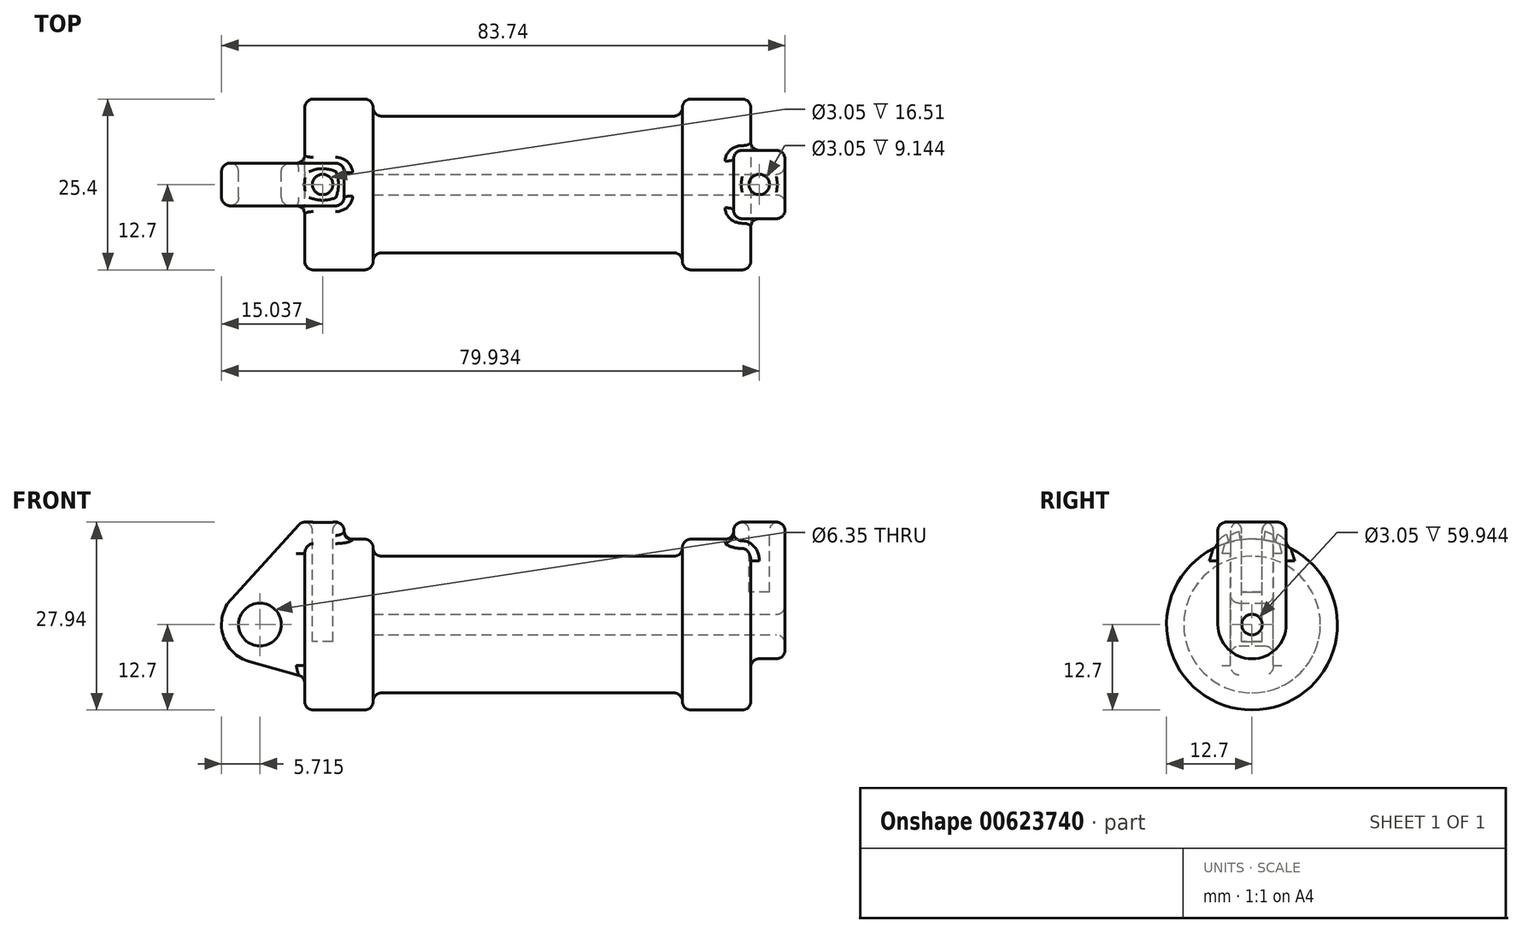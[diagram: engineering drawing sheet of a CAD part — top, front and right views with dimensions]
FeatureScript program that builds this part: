
annotation { "Feature Type Name" : "Feature", "Feature Type Description" : "" }
export const myFeature = defineFeature(function(context is Context, id is Id, definition is map)
    precondition{}
    {
        {
            var Q0;
            Q0=qCreatedBy(makeId("Front.planeOp"),FACE);
            var sketch = newSketch(context, id + "F0", { "sketchPlane" : qUnion([Q0])});
            skLineSegment(sketch, "E0", {"start": v(0, 0) * mm, "end": v(0, 12.7) * mm});
            skLineSegment(sketch, "E1", {"start": v(0, 12.7) * mm, "end": v(10.16, 12.7) * mm});
            skLineSegment(sketch, "E2", {"start": v(10.16, 12.7) * mm, "end": v(10.16, 10.16) * mm});
            skLineSegment(sketch, "E3", {"start": v(10.16, 10.16) * mm, "end": v(56.13, 10.16) * mm});
            skLineSegment(sketch, "E4", {"start": v(56.13, 10.16) * mm, "end": v(56.13, 12.7) * mm});
            skLineSegment(sketch, "E5", {"start": v(56.13, 12.7) * mm, "end": v(66.3, 12.7) * mm});
            skLineSegment(sketch, "E6", {"start": v(66.3, 12.7) * mm, "end": v(66.3, 0) * mm});
            skLineSegment(sketch, "E7", {"start": v(66.3, 0) * mm, "end": v(0, 0) * mm});
            skLineSegment(sketch, "E8", {"start": v(5.84, 15.24) * mm, "end": v(-0.5, 15.24) * mm});
            skLineSegment(sketch, "E9", {"start": v(-0.5, 15.24) * mm, "end": v(-10.88, 3.85) * mm});
            skLineSegment(sketch, "E10", {"start": v(0, 0) * mm, "end": v(-6.65, 0) * mm});
            skCircle(sketch, "E11", {"center": v(-6.65, 0) * mm, "radius": 5.72 * mm});
            skCircle(sketch, "E12", {"center": v(-6.65, 0) * mm, "radius": 3.18 * mm});
            skLineSegment(sketch, "E13", {"start": v(5.84, 15.24) * mm, "end": v(5.84, -9.4) * mm});
            skLineSegment(sketch, "E14", {"start": v(5.84, -9.4) * mm, "end": v(-8.18, -5.5) * mm});
            skSolve(sketch);
        }
        {
            var Q0;
            {var subQ1=sQuery(id+"F0.wireOp",EDGE,"E0");Q0=makeQuery(id+"F0.imprint","IMPRINT",FACE,{"disambiguationData":[TD([[makeQuery(id+"F0.imprint","IMPRINT",EDGE,{"derivedFrom":subQ1}),1.0]])]});}
            var Q1;
            {var subQ0=sQuery(id+"F0.wireOp",EDGE,"E14");Q1=makeQuery(id+"F0.imprint","IMPRINT",FACE,{"disambiguationData":[TD([[makeQuery(id+"F0.imprint","IMPRINT",EDGE,{"derivedFrom":subQ0}),-1.0]])]});}
            var Q2;
            {var subQ0=sQuery(id+"F0.wireOp",EDGE,"E0");Q2=makeQuery(id+"F0.imprint","IMPRINT",FACE,{"disambiguationData":[TD([[makeQuery(id+"F0.imprint","IMPRINT",EDGE,{"derivedFrom":subQ0}),-1.0]])]});}
            var Q3;
            {var subQ5=sQuery(id+"F0.wireOp",EDGE,"E12");Q3=makeQuery(id+"F0.imprint","IMPRINT",FACE,{"disambiguationData":[TD([[makeQuery(id+"F0.imprint","IMPRINT",EDGE,{"derivedFrom":subQ5}),-1.0]])]});}
            extrude(context, id + "F1", {"entities" : qUnion([Q0, Q1, Q2, Q3]), "endBound" : BoundingType.SYMMETRIC, "depth" : 6.35 * mm, "offsetDistance" : 25.4 * mm});
        }
        {
            var Q0;
            {var subQ0=sQuery(id+"F0.wireOp",EDGE,"E0");Q0=makeQuery(id+"F0.imprint","IMPRINT",FACE,{"disambiguationData":[TD([[makeQuery(id+"F0.imprint","IMPRINT",EDGE,{"derivedFrom":subQ0}),-1.0]])]});}
            var Q1;
            {var subQ0=sQuery(id+"F0.wireOp",EDGE,"E2");Q1=makeQuery(id+"F0.imprint","IMPRINT",FACE,{"disambiguationData":[TD([[makeQuery(id+"F0.imprint","IMPRINT",EDGE,{"derivedFrom":subQ0}),-1.0]])]});}
            var Q2;
            Q2=sQuery(id+"F0.wireOp",EDGE,"E7");
            revolve(context, id + "F2", {"operationType" : NewBodyOperationType.ADD, "entities" : qUnion([Q0, Q1]), "axis" : qUnion([Q2]), "revolveType" : RevolveType.FULL});
        }
        {
            var Q0;
            Q0=makeQuery(id+"F2.opRevolve","SWEPT_FACE",FACE,{"disambiguationData":[OSD([sQuery(id+"F0.wireOp",EDGE,"E6")])]});
            var sketch = newSketch(context, id + "F3", { "sketchPlane" : qUnion([Q0])});
            skCircle(sketch, "E15.0", {"center": v(0, 0) * mm, "radius": 12.7 * mm});
            skLineSegment(sketch, "E15.1", {"start": v(3.18, 15.24) * mm, "end": v(3.18, 12.3) * mm});
            skLineSegment(sketch, "E15.2", {"start": v(-3.18, 15.24) * mm, "end": v(3.17, 15.24) * mm});
            skLineSegment(sketch, "E15.3", {"start": v(-3.18, 15.24) * mm, "end": v(-3.18, 12.3) * mm});
            skLineSegment(sketch, "E16", {"start": v(0, 15.24) * mm, "end": v(0, -12.7) * mm, "construction": true});
            skCircle(sketch, "E17", {"center": v(0, 0) * mm, "radius": 1.52 * mm});
            skCircle(sketch, "E18", {"center": v(0, 0) * mm, "radius": 5.08 * mm});
            skLineSegment(sketch, "E19", {"start": v(5.08, 0) * mm, "end": v(5.08, 15.24) * mm});
            skLineSegment(sketch, "E20", {"start": v(5.08, 15.24) * mm, "end": v(3.18, 15.24) * mm});
            skLineSegment(sketch, "E21.MirrorCS", {"start": v(-5.08, 0) * mm, "end": v(-5.08, 15.24) * mm});
            skLineSegment(sketch, "E22.MirrorCS", {"start": v(-5.08, 15.24) * mm, "end": v(-3.18, 15.24) * mm});
            skSolve(sketch);
        }
        {
            var Q0;
            {var subQ0=sQuery(id+"F3.wireOp",EDGE,"E15.1");Q0=makeQuery(id+"F3.imprint","IMPRINT",FACE,{"disambiguationData":[TD([[makeQuery(id+"F3.imprint","IMPRINT",EDGE,{"derivedFrom":subQ0}),1.0]])]});}
            var Q1;
            {var subQ0=sQuery(id+"F3.wireOp",EDGE,"E15.1");Q1=makeQuery(id+"F3.imprint","IMPRINT",FACE,{"disambiguationData":[TD([[makeQuery(id+"F3.imprint","IMPRINT",EDGE,{"derivedFrom":subQ0}),-1.0]])]});}
            var Q2;
            {var subQ0=sQuery(id+"F3.wireOp",EDGE,"E15.3");Q2=makeQuery(id+"F3.imprint","IMPRINT",FACE,{"disambiguationData":[TD([[makeQuery(id+"F3.imprint","IMPRINT",EDGE,{"derivedFrom":subQ0}),-1.0]])]});}
            extrude(context, id + "F4", {"entities" : qUnion([Q0, Q1, Q2]), "operationType" : NewBodyOperationType.ADD, "oppositeDirection" : true, "depth" : 2.54 * mm, "offsetDistance" : 25.4 * mm});
        }
        {
            var Q0;
            Q0=makeQuery(id+"F3.imprint","IMPRINT",FACE,{"disambiguationData":[TD([[makeQuery(id+"F3.imprint","IMPRINT",EDGE,{"derivedFrom":sQuery(id+"F3.wireOp",EDGE,"E17")}),1.0]])]});
            var Q1;
            Q1=makeQuery(id+"F2.opRevolve","SWEPT_FACE",FACE,{"disambiguationData":[OSD([sQuery(id+"F0.wireOp",EDGE,"E2")])]});
            extrude(context, id + "F5", {"entities" : qUnion([Q0]), "operationType" : NewBodyOperationType.REMOVE, "endBound" : BoundingType.UP_TO_SURFACE, "oppositeDirection" : true, "depth" : 25.4 * mm, "endBoundEntityFace" : qUnion([Q1]), "offsetDistance" : 25.4 * mm});
        }
        {
            var Q0;
            {var subQ0=sQuery(id+"F3.wireOp",EDGE,"E15.3");Q0=makeQuery(id+"F3.imprint","IMPRINT",FACE,{"disambiguationData":[TD([[makeQuery(id+"F3.imprint","IMPRINT",EDGE,{"derivedFrom":subQ0}),-1.0]])]});}
            var Q1;
            {var subQ0=sQuery(id+"F3.wireOp",EDGE,"E15.1");Q1=makeQuery(id+"F3.imprint","IMPRINT",FACE,{"disambiguationData":[TD([[makeQuery(id+"F3.imprint","IMPRINT",EDGE,{"derivedFrom":subQ0}),-1.0]])]});}
            var Q2;
            {var subQ0=sQuery(id+"F3.wireOp",EDGE,"E15.1");Q2=makeQuery(id+"F3.imprint","IMPRINT",FACE,{"disambiguationData":[TD([[makeQuery(id+"F3.imprint","IMPRINT",EDGE,{"derivedFrom":subQ0}),1.0]])]});}
            var Q3;
            {var subQ5=sQuery(id+"F3.wireOp",EDGE,"E15.0");var subQ8=makeQuery(id+"F3.imprint","INTERSECT",VERTEX,{"derivedFrom":[subQ5,sQuery(id+"F3.wireOp",EDGE,"E15.1")]});Q3=makeQuery(id+"F3.imprint","IMPRINT",FACE,{"disambiguationData":[TD([[makeQuery(id+"F3.imprint","IMPRINT",EDGE,{"disambiguationData":[TD([[subQ8,1.0]])],"derivedFrom":subQ5}),1.0]])]});}
            var Q4;
            Q4=makeQuery(id+"F3.imprint","IMPRINT",FACE,{"disambiguationData":[TD([[makeQuery(id+"F3.imprint","IMPRINT",EDGE,{"derivedFrom":sQuery(id+"F3.wireOp",EDGE,"E17")}),-1.0]])]});
            extrude(context, id + "F6", {"entities" : qUnion([Q0, Q1, Q2, Q3, Q4]), "operationType" : NewBodyOperationType.ADD, "depth" : 5.08 * mm, "offsetDistance" : 25.4 * mm});
        }
        {
            var Q0;
            Q0=makeQuery(id+"F1.opExtrude","SWEPT_FACE",FACE,{"disambiguationData":[OSD([sQuery(id+"F0.wireOp",EDGE,"E8")])]});
            var sketch = newSketch(context, id + "F7", { "sketchPlane" : qUnion([Q0])});
            skCircle(sketch, "E23", {"center": v(2.67, 0) * mm, "radius": 1.52 * mm});
            skSolve(sketch);
        }
        {
            var Q0;
            Q0=makeQuery(id+"F7.imprint","IMPRINT",FACE,{"disambiguationData":[TD([[makeQuery(id+"F7.imprint","IMPRINT",EDGE,{"derivedFrom":sQuery(id+"F7.wireOp",EDGE,"E23")}),1.0]])]});
            extrude(context, id + "F8", {"entities" : qUnion([Q0]), "operationType" : NewBodyOperationType.REMOVE, "oppositeDirection" : true, "depth" : 17.78 * mm, "offsetDistance" : 25.4 * mm});
        }
        {
            var Q0;
            {var subQ0=sQuery(id+"F3.wireOp",EDGE,"E22.MirrorCS");var subQ1=sQuery(id+"F3.wireOp",EDGE,"E20");var subQ2=sQuery(id+"F3.wireOp",EDGE,"E15.2");Q0=makeQuery(id+"F6.boolean.opBoolean","MERGE",FACE,{"derivedFrom":[makeQuery(id+"F4.opExtrude","SWEPT_FACE",FACE,{"disambiguationData":[OSD([subQ2,subQ1,subQ0])]}),makeQuery(id+"F6.opExtrude","SWEPT_FACE",FACE,{"disambiguationData":[OSD([subQ2,subQ1,subQ0])]})]});}
            var sketch = newSketch(context, id + "F9", { "sketchPlane" : qUnion([Q0])});
            skLineSegment(sketch, "E24", {"start": v(63.75, 0) * mm, "end": v(71.37, 0) * mm, "construction": true});
            skCircle(sketch, "E25", {"center": v(67.56, 0) * mm, "radius": 1.52 * mm});
            skSolve(sketch);
        }
        {
            var Q0;
            Q0=makeQuery(id+"F9.imprint","IMPRINT",FACE,{"disambiguationData":[TD([[makeQuery(id+"F9.imprint","IMPRINT",EDGE,{"derivedFrom":sQuery(id+"F9.wireOp",EDGE,"E25")}),1.0]])]});
            extrude(context, id + "F10", {"entities" : qUnion([Q0]), "operationType" : NewBodyOperationType.REMOVE, "oppositeDirection" : true, "depth" : 10.4 * mm, "offsetDistance" : 25.4 * mm});
        }
        {
            var Q0;
            Q0=makeQuery(id+"F2.opRevolve","SWEPT_FACE",FACE,{"disambiguationData":[OSD([sQuery(id+"F0.wireOp",EDGE,"E3")])]});
            var Q1;
            Q1=makeQuery(id+"F6.opExtrude","CAP_FACE",FACE,{"disambiguationData":[OSD([sQuery(id+"F3.wireOp",EDGE,"E15.2"),sQuery(id+"F3.wireOp",EDGE,"E17"),sQuery(id+"F3.wireOp",EDGE,"E18"),sQuery(id+"F3.wireOp",EDGE,"E19"),sQuery(id+"F3.wireOp",EDGE,"E20"),sQuery(id+"F3.wireOp",EDGE,"E21.MirrorCS"),sQuery(id+"F3.wireOp",EDGE,"E22.MirrorCS")])],"isStart":false});
            var Q2;
            {var subQ0=sQuery(id+"F3.wireOp",EDGE,"E22.MirrorCS");var subQ1=sQuery(id+"F3.wireOp",EDGE,"E20");var subQ2=sQuery(id+"F3.wireOp",EDGE,"E15.2");Q2=makeQuery(id+"F6.boolean.opBoolean","MERGE",FACE,{"derivedFrom":[makeQuery(id+"F4.opExtrude","SWEPT_FACE",FACE,{"disambiguationData":[OSD([subQ2,subQ1,subQ0])]}),makeQuery(id+"F6.opExtrude","SWEPT_FACE",FACE,{"disambiguationData":[OSD([subQ2,subQ1,subQ0])]})]});}
            var Q3;
            Q3=makeQuery(id+"F4.boolean.opBoolean","MERGE",FACE,{"derivedFrom":[makeQuery(id+"F2.opRevolve","SWEPT_FACE",FACE,{"disambiguationData":[OSD([sQuery(id+"F0.wireOp",EDGE,"E6")])]}),makeQuery(id+"F4.opExtrude","CAP_FACE",FACE,{"disambiguationData":[OSD([sQuery(id+"F3.wireOp",EDGE,"E15.0"),sQuery(id+"F3.wireOp",EDGE,"E15.2"),sQuery(id+"F3.wireOp",EDGE,"E19"),sQuery(id+"F3.wireOp",EDGE,"E20"),sQuery(id+"F3.wireOp",EDGE,"E21.MirrorCS"),sQuery(id+"F3.wireOp",EDGE,"E22.MirrorCS")])],"isStart":true})]});
            var Q4;
            Q4=makeQuery(id+"F2.opRevolve","SWEPT_FACE",FACE,{"disambiguationData":[OSD([sQuery(id+"F0.wireOp",EDGE,"E5")])]});
            var Q5;
            Q5=makeQuery(id+"F2.opRevolve","SWEPT_FACE",FACE,{"disambiguationData":[OSD([sQuery(id+"F0.wireOp",EDGE,"E1")])]});
            var Q6;
            Q6=makeQuery(id+"F2.opRevolve","SWEPT_FACE",FACE,{"disambiguationData":[OSD([sQuery(id+"F0.wireOp",EDGE,"E0")])]});
            var Q7;
            Q7=makeQuery(id+"F1.opExtrude","CAP_FACE",FACE,{"disambiguationData":[OSD([sQuery(id+"F0.wireOp",EDGE,"E8"),sQuery(id+"F0.wireOp",EDGE,"E9"),sQuery(id+"F0.wireOp",EDGE,"E11"),sQuery(id+"F0.wireOp",EDGE,"E12"),sQuery(id+"F0.wireOp",EDGE,"E13"),sQuery(id+"F0.wireOp",EDGE,"E14")])],"isStart":false});
            var Q8;
            Q8=makeQuery(id+"F1.opExtrude","CAP_FACE",FACE,{"disambiguationData":[OSD([sQuery(id+"F0.wireOp",EDGE,"E8"),sQuery(id+"F0.wireOp",EDGE,"E9"),sQuery(id+"F0.wireOp",EDGE,"E11"),sQuery(id+"F0.wireOp",EDGE,"E12"),sQuery(id+"F0.wireOp",EDGE,"E13"),sQuery(id+"F0.wireOp",EDGE,"E14")])],"isStart":true});
            var Q9;
            Q9=makeQuery(id+"F1.opExtrude","SWEPT_FACE",FACE,{"disambiguationData":[OSD([sQuery(id+"F0.wireOp",EDGE,"E9")])]});
            var Q10;
            Q10=makeQuery(id+"F1.opExtrude","SWEPT_FACE",FACE,{"disambiguationData":[OSD([sQuery(id+"F0.wireOp",EDGE,"E8")])]});
            var Q11;
            Q11=makeQuery(id+"F1.opExtrude","SWEPT_FACE",FACE,{"disambiguationData":[OSD([sQuery(id+"F0.wireOp",EDGE,"E14")])]});
            var Q12;
            Q12=makeQuery(id+"F1.opExtrude","SWEPT_FACE",FACE,{"disambiguationData":[OSD([sQuery(id+"F0.wireOp",EDGE,"E12")])]});
            var Q13;
            Q13=makeQuery(id+"F4.opExtrude","CAP_FACE",FACE,{"disambiguationData":[OSD([sQuery(id+"F3.wireOp",EDGE,"E15.0"),sQuery(id+"F3.wireOp",EDGE,"E15.2"),sQuery(id+"F3.wireOp",EDGE,"E19"),sQuery(id+"F3.wireOp",EDGE,"E20"),sQuery(id+"F3.wireOp",EDGE,"E21.MirrorCS"),sQuery(id+"F3.wireOp",EDGE,"E22.MirrorCS")])],"isStart":false});
            var Q14;
            {var subQ0=sQuery(id+"F3.wireOp",EDGE,"E21.MirrorCS");Q14=makeQuery(id+"F6.boolean.opBoolean","MERGE",FACE,{"derivedFrom":[makeQuery(id+"F4.opExtrude","SWEPT_FACE",FACE,{"disambiguationData":[OSD([subQ0])]}),makeQuery(id+"F6.opExtrude","SWEPT_FACE",FACE,{"disambiguationData":[OSD([subQ0])]})]});}
            var Q15;
            Q15=makeQuery(id+"F6.opExtrude","SWEPT_FACE",FACE,{"disambiguationData":[OSD([sQuery(id+"F3.wireOp",EDGE,"E18")])]});
            var Q16;
            {var subQ0=sQuery(id+"F3.wireOp",EDGE,"E19");Q16=makeQuery(id+"F6.boolean.opBoolean","MERGE",FACE,{"derivedFrom":[makeQuery(id+"F4.opExtrude","SWEPT_FACE",FACE,{"disambiguationData":[OSD([subQ0])]}),makeQuery(id+"F6.opExtrude","SWEPT_FACE",FACE,{"disambiguationData":[OSD([subQ0])]})]});}
            var Q17;
            Q17=makeQuery(id+"F2.opRevolve","SWEPT_FACE",FACE,{"disambiguationData":[OSD([sQuery(id+"F0.wireOp",EDGE,"E4")])]});
            fillet(context, id + "F11", {"entities" : qUnion([Q0, Q1, Q2, Q3, Q4, Q5, Q6, Q7, Q8, Q9, Q10, Q11, Q12, Q13, Q14, Q15, Q16, Q17]), "radius" : 1.27 * mm, "tangentPropagation" : true, "allowEdgeOverflow" : false});
        }
    });
